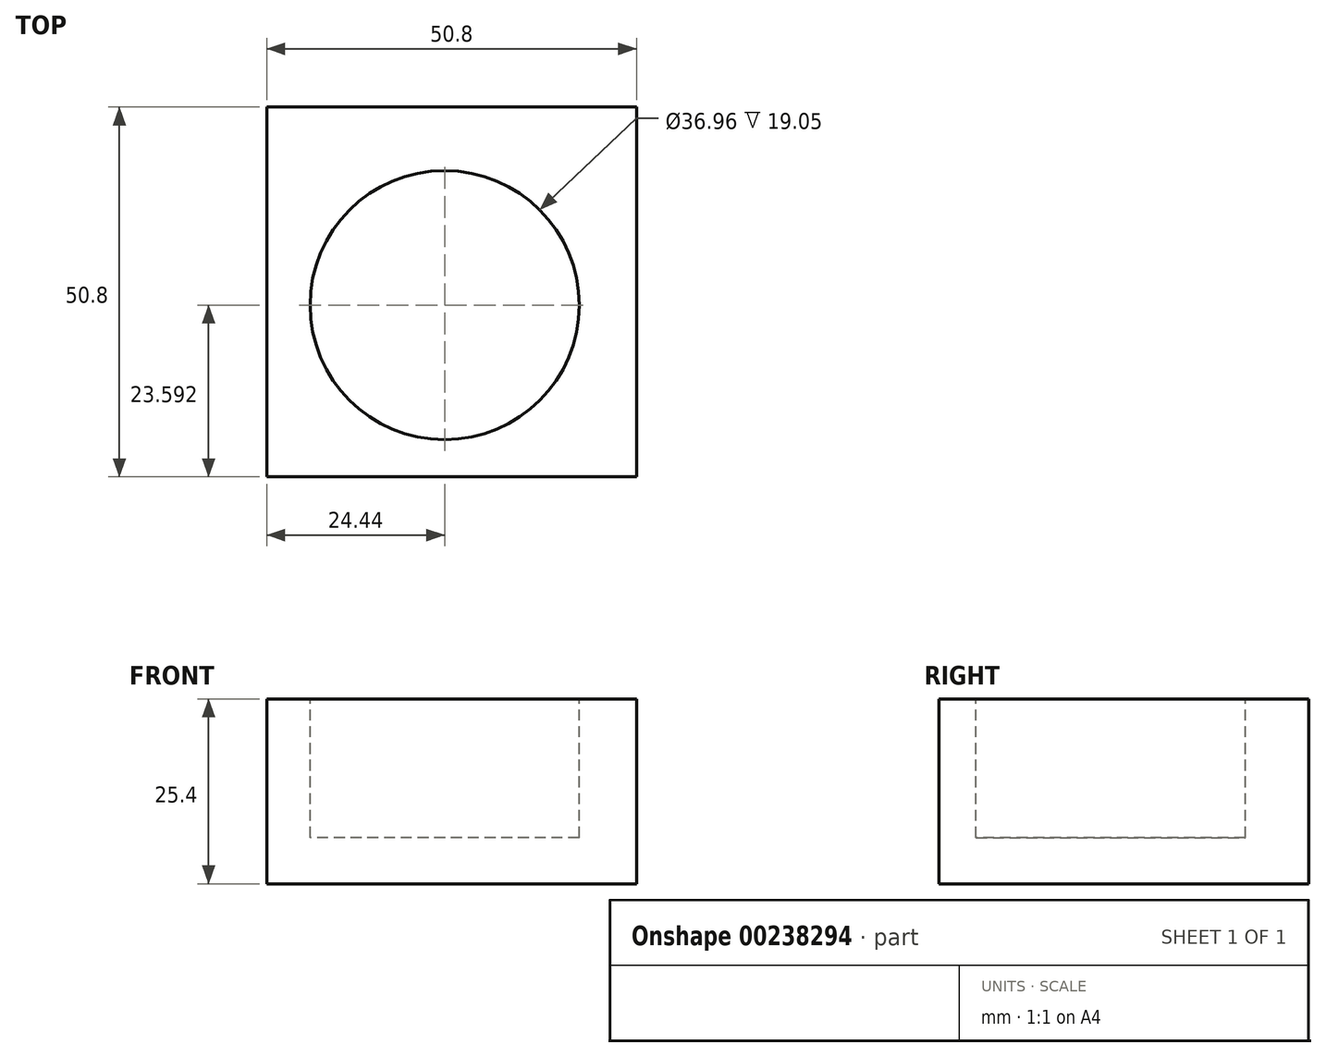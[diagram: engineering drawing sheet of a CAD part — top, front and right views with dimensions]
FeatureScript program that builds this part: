
annotation { "Feature Type Name" : "Feature", "Feature Type Description" : "" }
export const myFeature = defineFeature(function(context is Context, id is Id, definition is map)
    precondition{}
    {
        {
            var Q0;
            Q0=qCreatedBy(makeId("Top.planeOp"),FACE);
            var sketch = newSketch(context, id + "F0", { "sketchPlane" : qUnion([Q0])});
            skLineSegment(sketch, "E0.bottom", {"start": v(26.36, 0) * mm, "end": v(-24.44, 0) * mm});
            skLineSegment(sketch, "E0.top", {"start": v(26.36, 50.8) * mm, "end": v(-24.44, 50.8) * mm});
            skLineSegment(sketch, "E0.left", {"start": v(26.36, 0) * mm, "end": v(26.36, 50.8) * mm});
            skLineSegment(sketch, "E0.right", {"start": v(-24.44, 0) * mm, "end": v(-24.44, 50.8) * mm});
            skPoint(sketch, "E0.middle", {"position": v(0.96, 25.4) * mm});
            skSolve(sketch);
        }
        {
            var Q0;
            Q0=makeQuery(id+"F0.imprint","IMPRINT",FACE,{"disambiguationData":[TD([[makeQuery(id+"F0.imprint","IMPRINT",EDGE,{"derivedFrom":sQuery(id+"F0.wireOp",EDGE,"E0.bottom")}),-1.0]])]});
            extrude(context, id + "F1", {"entities" : qUnion([Q0]), "depth" : 25.4 * mm});
        }
        {
            var Q0;
            Q0=makeQuery(id+"F1.opExtrude","CAP_FACE",FACE,{"disambiguationData":[OSD([sQuery(id+"F0.wireOp",EDGE,"E0.bottom"),sQuery(id+"F0.wireOp",EDGE,"E0.top"),sQuery(id+"F0.wireOp",EDGE,"E0.left"),sQuery(id+"F0.wireOp",EDGE,"E0.right")])],"isStart":false});
            var sketch = newSketch(context, id + "F2", { "sketchPlane" : qUnion([Q0])});
            skCircle(sketch, "E1", {"center": v(0, 23.6) * mm, "radius": 18.48 * mm});
            skSolve(sketch);
        }
        {
            var Q0;
            Q0=makeQuery(id+"F2.imprint","IMPRINT",FACE,{"disambiguationData":[TD([[makeQuery(id+"F2.imprint","IMPRINT",EDGE,{"derivedFrom":sQuery(id+"F2.wireOp",EDGE,"E1")}),1.0]])]});
            var Q1;
            Q1=sQuery(id+"F2.wireOp",EDGE,"E1");
            extrude(context, id + "F3", {"entities" : qUnion([Q0]), "operationType" : NewBodyOperationType.REMOVE, "surfaceEntities" : qUnion([Q1]), "oppositeDirection" : true, "depth" : 19.05 * mm});
        }
    });
